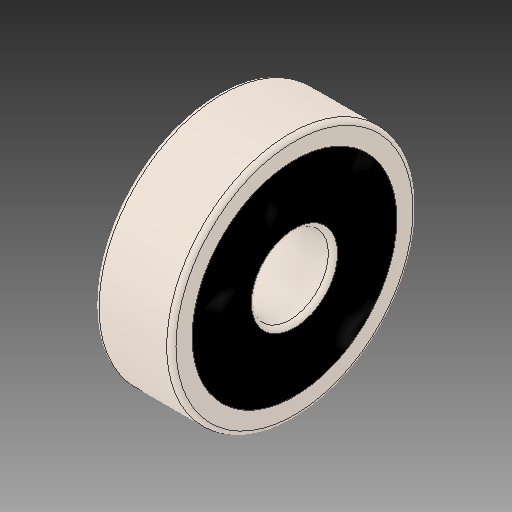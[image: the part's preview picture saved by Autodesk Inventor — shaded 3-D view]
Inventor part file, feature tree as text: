
AUTODESK INVENTOR PART (.ipt)
format: ipt  version: 2018 (Build 220112000, 112)  size: 2,314,240 bytes
history: imported  units: mm
features: other x22, sketch x2, imported_body x1
ambient origin geometry x8: Origin, YZ Plane, XZ Plane, XY Plane, X Axis, Y Axis, Z Axis, Center Point
bodies: Solid1 (imported_parasolid), Solid2 (imported_parasolid), Solid3 (imported_parasolid), Solid4 (imported_parasolid), Solid5 (imported_parasolid), Solid6 (imported_parasolid), Solid7 (imported_parasolid), Solid8 (imported_parasolid), Solid9 (imported_parasolid), Solid10 (imported_parasolid), Solid11 (imported_parasolid), Solid12 (imported_parasolid), Solid13 (imported_parasolid), Solid14 (imported_parasolid), Solid15 (imported_parasolid), Solid16 (imported_parasolid), Solid17 (imported_parasolid), Solid18 (imported_parasolid), Solid19 (imported_parasolid), Solid20 (imported_parasolid)
feature tree (25):
  other  "SKF 625_CPY_MIR1.ipt"
  other  "Solid1::SKF 625_CPY_MIR1.ipt"
  other  "Solid2::SKF 625_CPY_MIR1.ipt"
  other  "Solid3::SKF 625_CPY_MIR1.ipt"
  other  "Solid4::SKF 625_CPY_MIR1.ipt"
  other  "Solid5::SKF 625_CPY_MIR1.ipt"
  other  "Solid6::SKF 625_CPY_MIR1.ipt"
  other  "Solid7::SKF 625_CPY_MIR1.ipt"
  other  "Solid8::SKF 625_CPY_MIR1.ipt"
  other  "Solid9::SKF 625_CPY_MIR1.ipt"
  other  "Solid10::SKF 625_CPY_MIR1.ipt"
  other  "Solid11::SKF 625_CPY_MIR1.ipt"
  other  "Solid12::SKF 625_CPY_MIR1.ipt"
  other  "Solid13::SKF 625_CPY_MIR1.ipt"
  other  "Solid14::SKF 625_CPY_MIR1.ipt"
  other  "Solid15::SKF 625_CPY_MIR1.ipt"
  other  "Solid16::SKF 625_CPY_MIR1.ipt"
  other  "Solid17::SKF 625_CPY_MIR1.ipt"
  other  "Solid18::SKF 625_CPY_MIR1.ipt"
  other  "Solid19::SKF 625_CPY_MIR1.ipt"
  other  "Solid20::SKF 625_CPY_MIR1.ipt"
  other  "TaggingFeature1"
  sketch  "Sketch1"  dims[d0=10.0mm]
  sketch  "Sketch2"
  imported_body  NMx_Import_Brep_tag  [imported B-rep: ~49 faces, bbox_mm=None]
